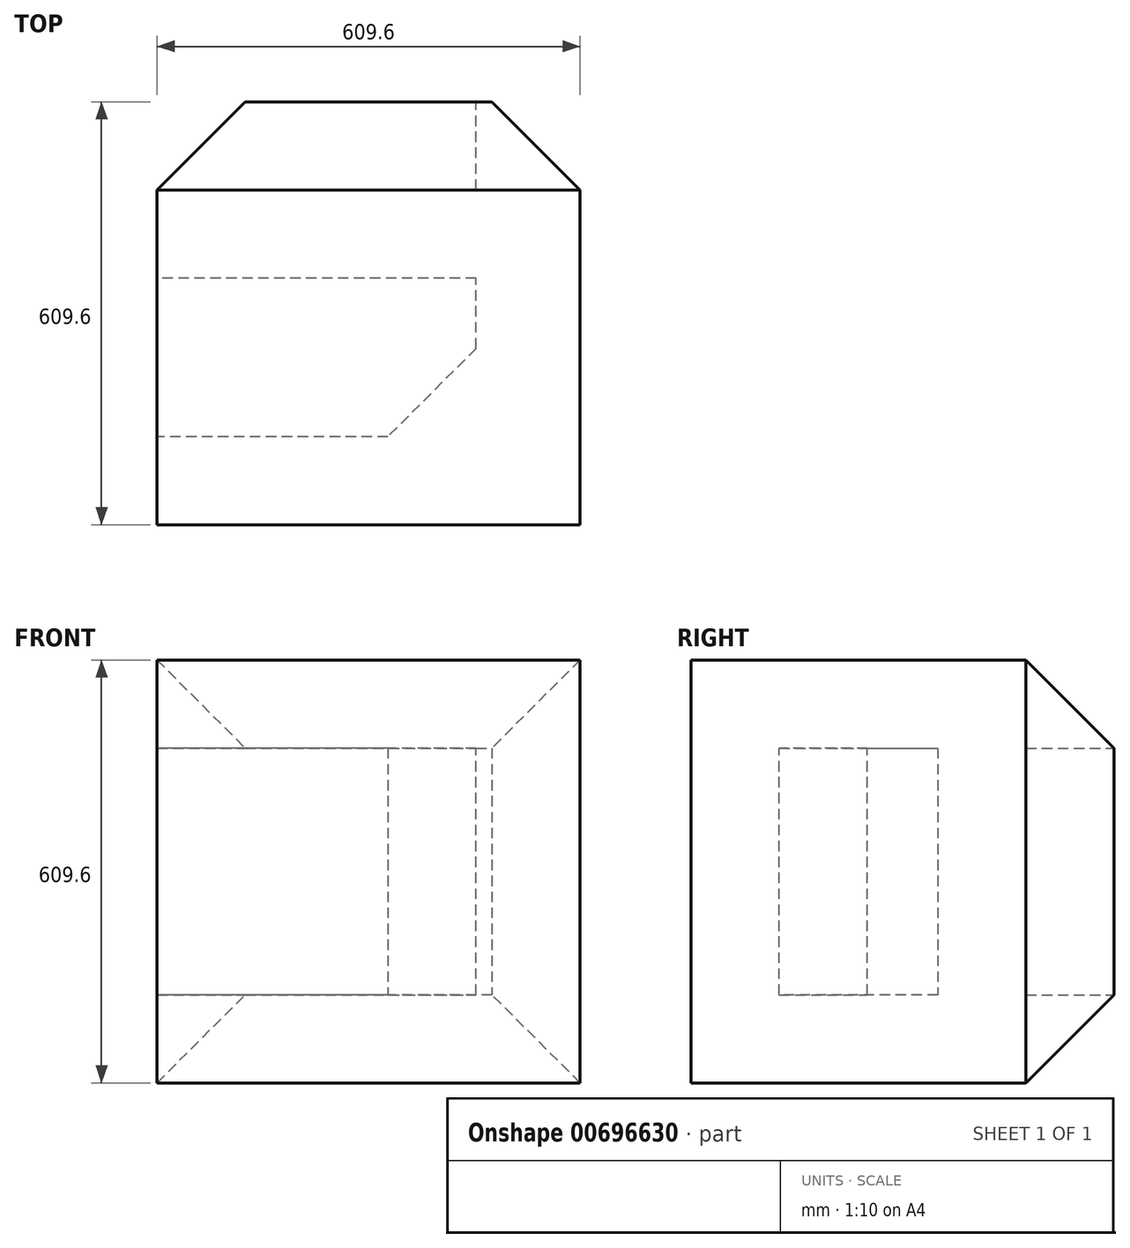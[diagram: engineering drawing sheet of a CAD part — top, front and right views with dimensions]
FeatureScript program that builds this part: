
annotation { "Feature Type Name" : "Feature", "Feature Type Description" : "" }
export const myFeature = defineFeature(function(context is Context, id is Id, definition is map)
    precondition{}
    {
        {
            var Q0;
            Q0=qCreatedBy(makeId("Top.planeOp"),FACE);
            var sketch = newSketch(context, id + "F0", { "sketchPlane" : qUnion([Q0])});
            skLineSegment(sketch, "E0.bottom", {"start": v(-23.66, 562.41) * mm, "end": v(585.94, 562.41) * mm});
            skLineSegment(sketch, "E0.top", {"start": v(-23.66, -47.19) * mm, "end": v(585.94, -47.19) * mm});
            skLineSegment(sketch, "E0.left", {"start": v(-23.66, 562.41) * mm, "end": v(-23.66, -47.19) * mm});
            skLineSegment(sketch, "E0.right", {"start": v(585.94, 562.41) * mm, "end": v(585.94, -47.19) * mm});
            skSolve(sketch);
        }
        {
            var Q0;
            Q0=makeQuery(id+"F0.imprint","IMPRINT",FACE,{"disambiguationData":[TD([[makeQuery(id+"F0.imprint","IMPRINT",EDGE,{"derivedFrom":sQuery(id+"F0.wireOp",EDGE,"E0.bottom")}),-1.0]])]});
            extrude(context, id + "F1", {"entities" : qUnion([Q0]), "depth" : 609.6 * mm, "offsetDistance" : 25.4 * mm});
        }
        {
            var Q0;
            Q0=makeQuery(id+"F1.opExtrude","SWEPT_FACE",FACE,{"disambiguationData":[OSD([sQuery(id+"F0.wireOp",EDGE,"E0.bottom")])]});
            chamfer(context, id + "F2", {"entities" : qUnion([Q0]), "width" : 127 * mm, "tangentPropagation" : true});
        }
        {
            var Q0;
            Q0=makeQuery(id+"F1.opExtrude","SWEPT_FACE",FACE,{"disambiguationData":[OSD([sQuery(id+"F0.wireOp",EDGE,"E0.left")])]});
            var sketch = newSketch(context, id + "F3", { "sketchPlane" : qUnion([Q0])});
            skLineSegment(sketch, "E1.0", {"start": v(-79.81, 482.6) * mm, "end": v(-308.41, 482.6) * mm});
            skLineSegment(sketch, "E1.1", {"start": v(-79.81, 127) * mm, "end": v(-79.81, 482.6) * mm});
            skLineSegment(sketch, "E1.2", {"start": v(-308.41, 127) * mm, "end": v(-79.81, 127) * mm});
            skLineSegment(sketch, "E1.3", {"start": v(-308.41, 482.6) * mm, "end": v(-308.41, 127) * mm});
            skLineSegment(sketch, "E2.bottom", {"start": v(-308.41, 127) * mm, "end": v(-786.7, 127) * mm});
            skLineSegment(sketch, "E2.top", {"start": v(-308.41, 482.6) * mm, "end": v(-786.7, 482.6) * mm});
            skLineSegment(sketch, "E2.left", {"start": v(-308.41, 127) * mm, "end": v(-308.41, 482.6) * mm});
            skLineSegment(sketch, "E2.right", {"start": v(-786.7, 127) * mm, "end": v(-786.7, 482.6) * mm});
            skSolve(sketch);
        }
        {
            var Q0;
            Q0=makeQuery(id+"F3.imprint","IMPRINT",FACE,{"disambiguationData":[TD([[makeQuery(id+"F3.imprint","IMPRINT",EDGE,{"derivedFrom":sQuery(id+"F3.wireOp",EDGE,"E1.0")}),1.0]])]});
            var Q1;
            {var subQ0=sQuery(id+"F3.wireOp",EDGE,"E2.left");Q1=makeQuery(id+"F3.imprint","IMPRINT",FACE,{"disambiguationData":[TD([[makeQuery(id+"F3.imprint","IMPRINT",EDGE,{"derivedFrom":subQ0}),1.0]])]});}
            var Q2;
            {var subQ0=sQuery(id+"F3.wireOp",EDGE,"E2.right");Q2=makeQuery(id+"F3.imprint","IMPRINT",FACE,{"disambiguationData":[TD([[makeQuery(id+"F3.imprint","IMPRINT",EDGE,{"derivedFrom":subQ0}),-1.0]])]});}
            extrude(context, id + "F4", {"entities" : qUnion([Q0, Q1, Q2]), "operationType" : NewBodyOperationType.REMOVE, "oppositeDirection" : true, "depth" : 459.74 * mm, "offsetDistance" : 25.4 * mm});
        }
        {
            var Q0;
            Q0=makeQuery(id+"F4.boolean.opBoolean","COPY",EDGE,{"derivedFrom":makeQuery(id+"F4.opExtrude","CAP_EDGE",EDGE,{"disambiguationData":[OSD([sQuery(id+"F3.wireOp",EDGE,"E1.1")])],"isStart":false})});
            chamfer(context, id + "F5", {"entities" : qUnion([Q0]), "width" : 127 * mm, "tangentPropagation" : true});
        }
    });
